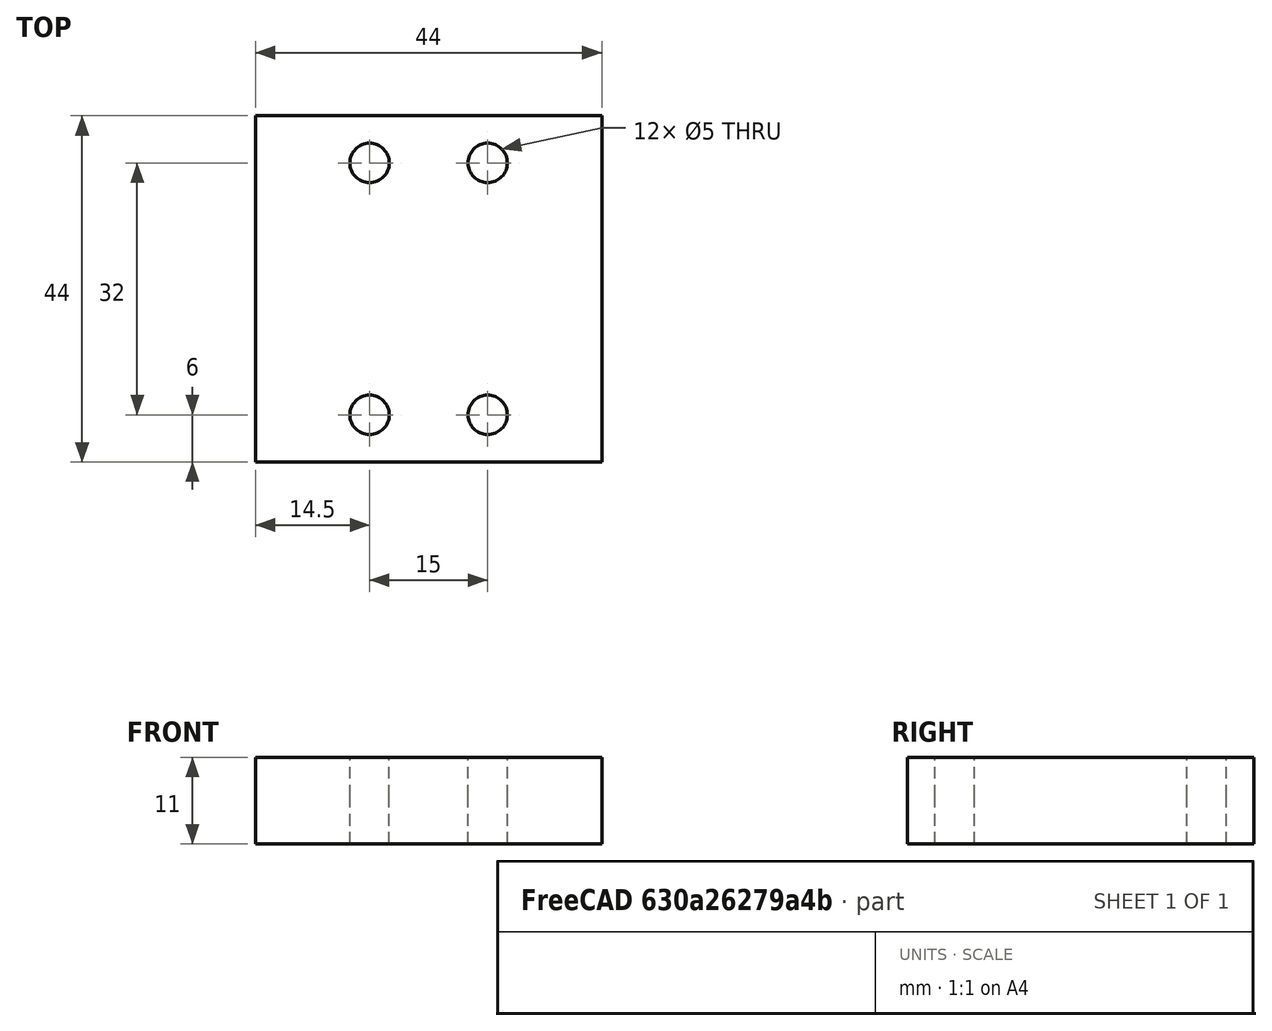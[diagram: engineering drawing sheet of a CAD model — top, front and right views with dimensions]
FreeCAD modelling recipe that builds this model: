
FCSTD DOCUMENT  (FreeCAD 0.16R)
Label: uper-part-with4holes-12mm
License: All rights reserved
LicenseURL: http://en.wikipedia.org/wiki/All_rights_reserved
objects: Part::Cylinder×8, Part::Cut×8, Part::Box×2, Part::MultiFuse×1
note: 19 computed .brp shape members not serialized (recipe doc carries the construction recipe); baked Part::Feature solids carry a one-line shape summary decoded from their .brp

FEATURE [Part::Box] Box  label="Cube"
  Height = 6
  Length = 44
  Width = 44
FEATURE [Part::Cylinder] Cylinder
  Angle = 360
  Height = 10
  Placement = pos=(14.5,6,0) rot=(0,0,1;0rad)
  Radius = 2.5
FEATURE [Part::Cylinder] Cylinder001
  Angle = 360
  Height = 10
  Placement = pos=(29.5,6,0) rot=(0,0,1;0rad)
  Radius = 2.5
FEATURE [Part::Cylinder] Cylinder002
  Angle = 360
  Height = 10
  Placement = pos=(14.5,38,0) rot=(0,0,1;0rad)
  Radius = 2.5
FEATURE [Part::Cylinder] Cylinder003
  Angle = 360
  Height = 10
  Placement = pos=(29.5,38,0) rot=(0,0,1;0rad)
  Radius = 2.5
FEATURE [Part::Cut] Cut
  Base = -> Box
  Tool = -> Cylinder
FEATURE [Part::Cut] Cut001
  Base = -> Cut
  Tool = -> Cylinder001
FEATURE [Part::Cut] Cut002
  Base = -> Cut001
  Tool = -> Cylinder003
FEATURE [Part::Cut] Cut003
  Base = -> Cut002
  Tool = -> Cylinder002
FEATURE [Part::Box] Box001  label="Cube001"
  Height = 6
  Length = 44
  Width = 44
FEATURE [Part::Cylinder] Cylinder004
  Angle = 360
  Height = 10
  Placement = pos=(14.5,6,0) rot=(0,0,1;0rad)
  Radius = 2.5
FEATURE [Part::Cylinder] Cylinder005
  Angle = 360
  Height = 10
  Placement = pos=(29.5,6,0) rot=(0,0,1;0rad)
  Radius = 2.5
FEATURE [Part::Cylinder] Cylinder006
  Angle = 360
  Height = 10
  Placement = pos=(14.5,38,0) rot=(0,0,1;0rad)
  Radius = 2.5
FEATURE [Part::Cylinder] Cylinder007
  Angle = 360
  Height = 10
  Placement = pos=(29.5,38,0) rot=(0,0,1;0rad)
  Radius = 2.5
FEATURE [Part::Cut] Cut004
  Base = -> Box001
  Tool = -> Cylinder004
FEATURE [Part::Cut] Cut005
  Base = -> Cut004
  Tool = -> Cylinder005
FEATURE [Part::Cut] Cut006
  Base = -> Cut005
  Tool = -> Cylinder007
FEATURE [Part::Cut] Cut007
  Base = -> Cut006
  Placement = pos=(0,0,5) rot=(0,0,1;0rad)
  Tool = -> Cylinder006
FEATURE [Part::MultiFuse] Fusion
  Shapes = -> [Cut003,Cut007]
